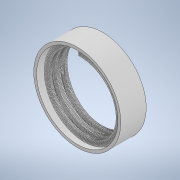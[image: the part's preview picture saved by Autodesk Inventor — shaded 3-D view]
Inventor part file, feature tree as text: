
AUTODESK INVENTOR PART (.ipt)
format: ipt  version: 2022 (Build 260153000, 153)  size: 247,808 bytes
history: native  units: mm
features: other x2, extrude x1, sketch x1
ambient origin geometry x8: Origin, YZ Plane, XZ Plane, XY Plane, X Axis, Y Axis, Z Axis, Center Point
bodies: Solid1 (feature_tree)
feature tree (4):
  other  "vial thread insert"
  extrude  "Extrusion1"  Depth=9.0mm TaperAngle=0.0deg
  sketch  "Sketch1"  dims[d0=1.0mm d1=9.0mm d2=0.0mm]
  other  "MeshFeature1"
